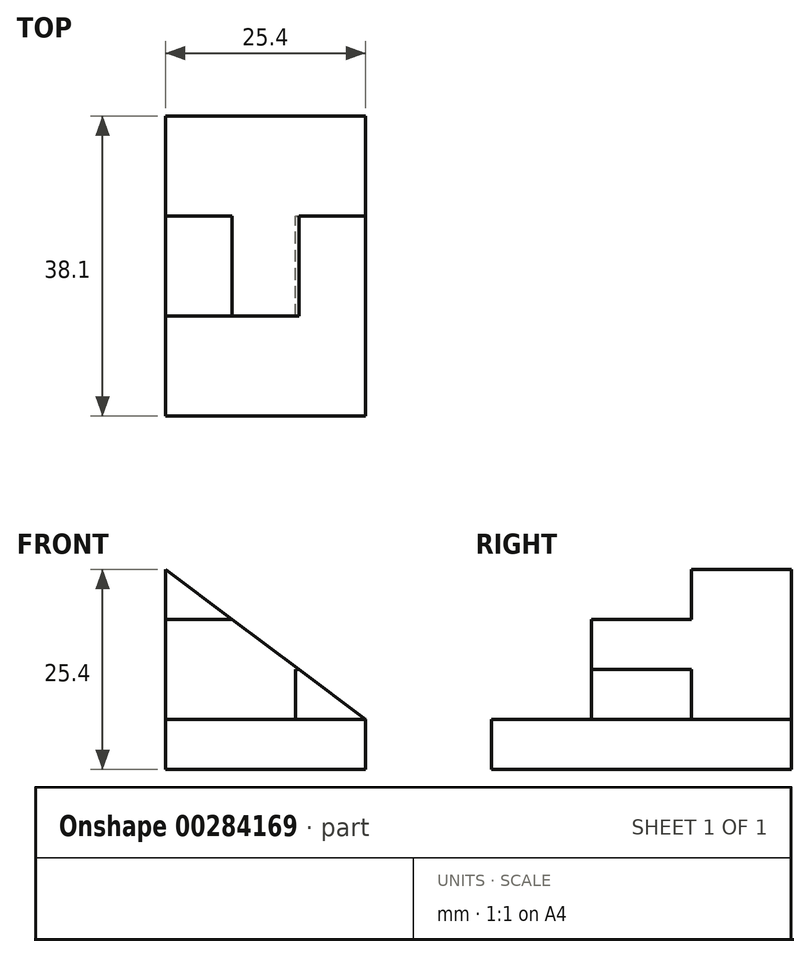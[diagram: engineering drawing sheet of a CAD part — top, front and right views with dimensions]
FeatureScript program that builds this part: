
annotation { "Feature Type Name" : "Feature", "Feature Type Description" : "" }
export const myFeature = defineFeature(function(context is Context, id is Id, definition is map)
    precondition{}
    {
        {
            var Q0;
            Q0=qCreatedBy(makeId("Front.planeOp"),FACE);
            var sketch = newSketch(context, id + "F0", { "sketchPlane" : qUnion([Q0])});
            skLineSegment(sketch, "E0.bottom", {"start": v(-25.4, 0) * mm, "end": v(0, 0) * mm});
            skLineSegment(sketch, "E0.top", {"start": v(-25.4, 6.35) * mm, "end": v(0, 6.35) * mm});
            skLineSegment(sketch, "E0.left", {"start": v(-25.4, 0) * mm, "end": v(-25.4, 6.35) * mm});
            skLineSegment(sketch, "E0.right", {"start": v(0, 0) * mm, "end": v(0, 6.35) * mm});
            skSolve(sketch);
        }
        {
            var Q0;
            Q0=makeQuery(id+"F0.imprint","IMPRINT",FACE,{"disambiguationData":[TD([[makeQuery(id+"F0.imprint","IMPRINT",EDGE,{"derivedFrom":sQuery(id+"F0.wireOp",EDGE,"E0.bottom")}),1.0]])]});
            extrude(context, id + "F1", {"entities" : qUnion([Q0]), "depth" : 38.1 * mm});
        }
        {
            var Q0;
            Q0=qCreatedBy(makeId("Right.planeOp"),FACE);
            var sketch = newSketch(context, id + "F2", { "sketchPlane" : qUnion([Q0])});
            skLineSegment(sketch, "E1", {"start": v(0, 6.35) * mm, "end": v(0, 25.4) * mm});
            skLineSegment(sketch, "E2", {"start": v(0, 25.4) * mm, "end": v(-12.7, 25.4) * mm});
            skLineSegment(sketch, "E3", {"start": v(-12.7, 25.4) * mm, "end": v(-12.7, 19.05) * mm});
            skLineSegment(sketch, "E4", {"start": v(-12.7, 19.05) * mm, "end": v(-25.4, 19.05) * mm});
            skLineSegment(sketch, "E5", {"start": v(-25.4, 19.05) * mm, "end": v(-25.4, 12.7) * mm});
            skLineSegment(sketch, "E6", {"start": v(-25.4, 12.7) * mm, "end": v(-12.7, 12.7) * mm});
            skLineSegment(sketch, "E7", {"start": v(-12.7, 12.7) * mm, "end": v(-12.7, 6.35) * mm});
            skLineSegment(sketch, "E8", {"start": v(-12.7, 6.35) * mm, "end": v(0, 6.35) * mm});
            skLineSegment(sketch, "E9", {"start": v(-25.4, 6.35) * mm, "end": v(-25.4, 12.7) * mm});
            skLineSegment(sketch, "E10", {"start": v(-25.4, 6.35) * mm, "end": v(-12.7, 6.35) * mm});
            skSolve(sketch);
        }
        {
            var Q0;
            Q0 = qSketchRegion(id + "F2", true);
            extrude(context, id + "F3", {"entities" : qUnion([Q0]), "oppositeDirection" : true, "depth" : 25.4 * mm});
        }
        {
            var Q0;
            Q0=qCreatedBy(makeId("Front.planeOp"),FACE);
            var sketch = newSketch(context, id + "F4", { "sketchPlane" : qUnion([Q0])});
            skLineSegment(sketch, "E11", {"start": v(0, 6.35) * mm, "end": v(-25.4, 25.4) * mm});
            skLineSegment(sketch, "E12", {"start": v(-25.4, 25.4) * mm, "end": v(0, 25.4) * mm});
            skLineSegment(sketch, "E13", {"start": v(0, 25.4) * mm, "end": v(0, 6.35) * mm});
            skSolve(sketch);
        }
        {
            var Q0;
            Q0 = qSketchRegion(id + "F4", true);
            extrude(context, id + "F5", {"entities" : qUnion([Q0]), "operationType" : NewBodyOperationType.REMOVE, "depth" : 38.1 * mm});
        }
        {
            var Q0;
            Q0=qCreatedBy(makeId("Right.planeOp"),FACE);
            var sketch = newSketch(context, id + "F6", { "sketchPlane" : qUnion([Q0])});
            skLineSegment(sketch, "E14.bottom", {"start": v(-25.4, 6.35) * mm, "end": v(-12.7, 6.35) * mm});
            skLineSegment(sketch, "E14.top", {"start": v(-25.4, 12.7) * mm, "end": v(-12.7, 12.7) * mm});
            skLineSegment(sketch, "E14.left", {"start": v(-25.4, 6.35) * mm, "end": v(-25.4, 12.7) * mm});
            skLineSegment(sketch, "E14.right", {"start": v(-12.7, 6.35) * mm, "end": v(-12.7, 12.7) * mm});
            skSolve(sketch);
        }
        {
            var Q0;
            Q0 = qSketchRegion(id + "F6", true);
            extrude(context, id + "F7", {"entities" : qUnion([Q0]), "operationType" : NewBodyOperationType.REMOVE, "oppositeDirection" : true, "depth" : 8.9 * mm});
        }
    });
